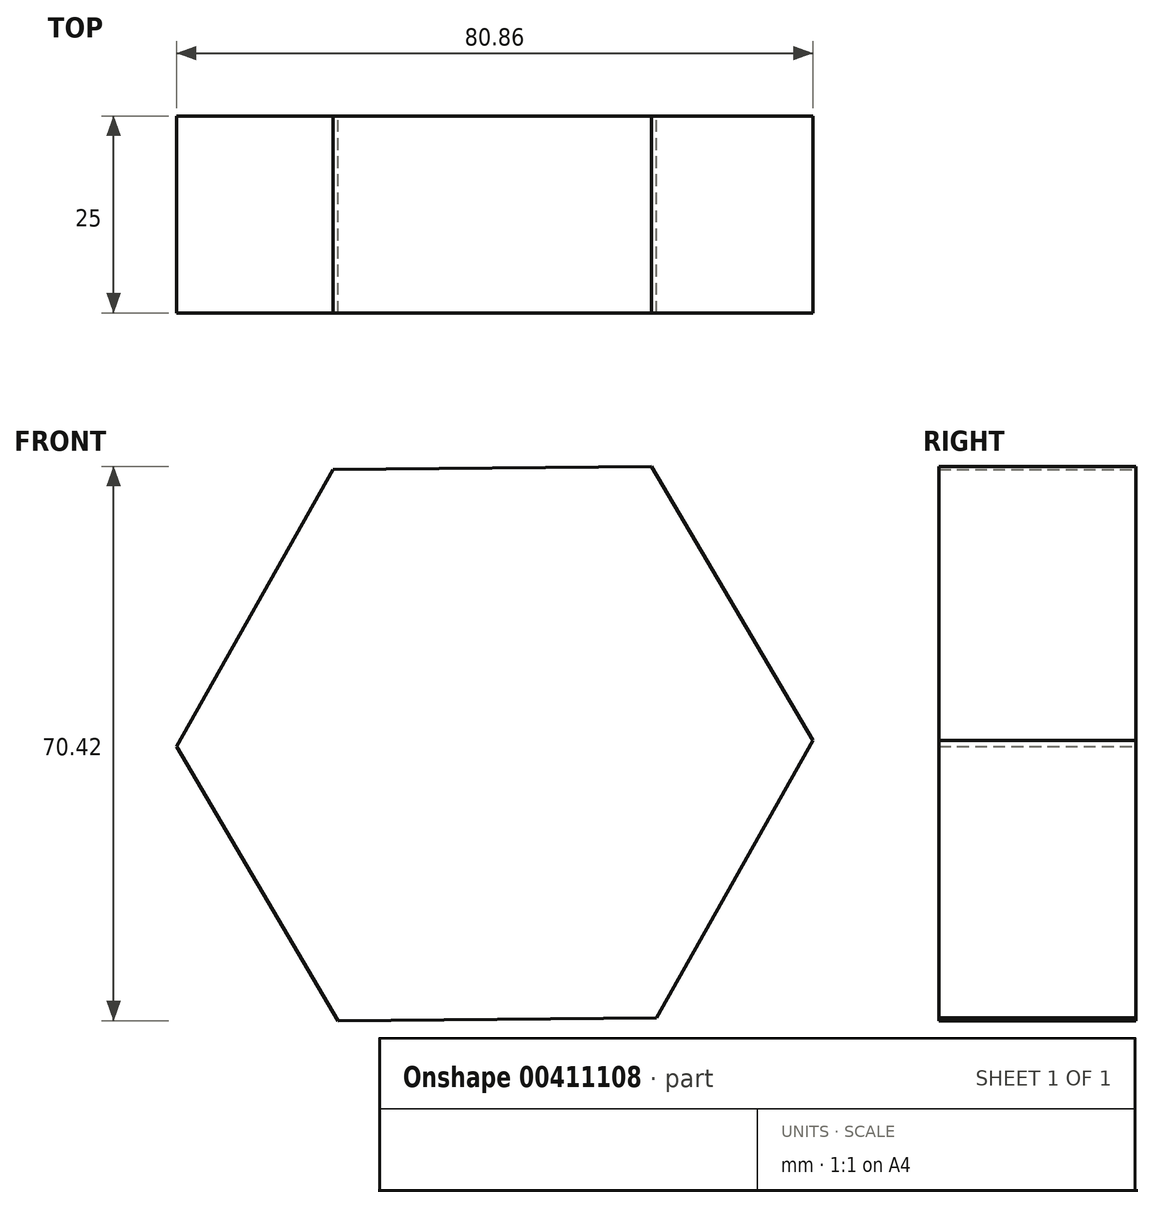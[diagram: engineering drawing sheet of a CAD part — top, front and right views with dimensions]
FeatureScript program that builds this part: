
annotation { "Feature Type Name" : "Feature", "Feature Type Description" : "" }
export const myFeature = defineFeature(function(context is Context, id is Id, definition is map)
    precondition{}
    {
        {
            var Q0;
            Q0=qCreatedBy(makeId("Front.planeOp"),FACE);
            var sketch = newSketch(context, id + "F0", { "sketchPlane" : qUnion([Q0])});
            skCircle(sketch, "E0", {"center": v(-53, 29.3) * mm, "radius": 40 * mm});
            skLineSegment(sketch, "E1.bottom", {"start": v(-12.08, 51.29) * mm, "end": v(0, 51.29) * mm});
            skLineSegment(sketch, "E1.top", {"start": v(-12.08, -74.46) * mm, "end": v(0, -74.46) * mm});
            skLineSegment(sketch, "E1.left", {"start": v(-12.08, 51.29) * mm, "end": v(-12.08, -74.46) * mm});
            skLineSegment(sketch, "E1.right", {"start": v(0, 51.29) * mm, "end": v(0, -74.46) * mm});
            skPoint(sketch, "E2.orphan", {"position": v(-12.08, -11.59) * mm});
            skLineSegment(sketch, "E3.left", {"start": v(-12.08, -11.59) * mm, "end": v(-12.08, 13.26) * mm});
            skPoint(sketch, "E3.middle", {"position": v(-24.88, 0.84) * mm});
            skLineSegment(sketch, "E4.0", {"start": v(-72.88, -5.92) * mm, "end": v(-93.42, 28.9) * mm});
            skLineSegment(sketch, "E4.1", {"start": v(-93.42, 28.9) * mm, "end": v(-73.54, 64.12) * mm});
            skLineSegment(sketch, "E4.2", {"start": v(-73.54, 64.12) * mm, "end": v(-33.1, 64.5) * mm});
            skLineSegment(sketch, "E4.3", {"start": v(-33.1, 64.5) * mm, "end": v(-12.56, 29.67) * mm});
            skLineSegment(sketch, "E4.4", {"start": v(-12.56, 29.67) * mm, "end": v(-32.44, -5.53) * mm});
            skLineSegment(sketch, "E4.5", {"start": v(-32.44, -5.53) * mm, "end": v(-72.88, -5.92) * mm});
            skPoint(sketch, "E4.0.midPoint", {"position": v(-83.15, 11.5) * mm});
            skLineSegment(sketch, "E5", {"start": v(-32.44, -5.53) * mm, "end": v(-12.08, 6.48) * mm});
            skLineSegment(sketch, "E6", {"start": v(-12.08, 6.48) * mm, "end": v(-32.44, -5.53) * mm});
            skLineSegment(sketch, "E7", {"start": v(-32.44, -5.53) * mm, "end": v(-51.42, -16.73) * mm});
            skLineSegment(sketch, "E8", {"start": v(-51.42, -16.73) * mm, "end": v(-72.88, -5.92) * mm});
            skLineSegment(sketch, "E9.0", {"start": v(-37.41, 61.96) * mm, "end": v(-16.86, 27.13) * mm});
            skSolve(sketch);
        }
        {
            var Q0;
            {var subQ0=sQuery(id+"F0.wireOp",EDGE,"E0");var subQ1=makeQuery(id+"F0.imprint","INTERSECT",VERTEX,{"derivedFrom":[subQ0,sQuery(id+"F0.wireOp",EDGE,"cFNFvZNz-d46b-ASLS-Qc6U-PmH5xnYiagzZ")]});Q0=makeQuery(id+"F0.imprint","IMPRINT",FACE,{"disambiguationData":[TD([[makeQuery(id+"F0.imprint","IMPRINT",EDGE,{"disambiguationData":[TD([[subQ1,1.0]])],"derivedFrom":subQ0}),1.0]])]});}
            var Q1;
            {var subQ0=sQuery(id+"F0.wireOp",EDGE,"E1.left");var subQ1=sQuery(id+"F0.wireOp",EDGE,"E0");var subQ2=makeQuery(id+"F0.imprint","INTERSECT",VERTEX,{"disambiguationData":[OD(0.0)],"derivedFrom":[subQ1,subQ0]});Q1=makeQuery(id+"F0.imprint","IMPRINT",FACE,{"disambiguationData":[TD([[makeQuery(id+"F0.imprint","IMPRINT",EDGE,{"disambiguationData":[TD([[subQ2,1.0]])],"derivedFrom":subQ1}),1.0]])]});}
            var Q2;
            {var subQ0=sQuery(id+"F0.wireOp",EDGE,"cFNFvZNz-d46b-ASLS-Qc6U-PmH5xnYiagzZ");var subQ1=sQuery(id+"F0.wireOp",EDGE,"E0");var subQ2=makeQuery(id+"F0.imprint","INTERSECT",VERTEX,{"derivedFrom":[subQ1,subQ0]});Q2=makeQuery(id+"F0.imprint","IMPRINT",FACE,{"disambiguationData":[TD([[makeQuery(id+"F0.imprint","IMPRINT",EDGE,{"disambiguationData":[TD([[subQ2,-1.0]])],"derivedFrom":subQ1}),-1.0]])]});}
            var Q3;
            {var subQ3=sQuery(id+"F0.wireOp",EDGE,"IICF6Ew8-t1GV-zMsd-5ZgM-YvJbXeU4h0B7");Q3=makeQuery(id+"F0.imprint","IMPRINT",FACE,{"disambiguationData":[TD([[makeQuery(id+"F0.imprint","IMPRINT",EDGE,{"derivedFrom":subQ3}),-1.0]])]});}
            var Q4;
            {var subQ6=sQuery(id+"F0.wireOp",EDGE,"VdmRn4Ws-3Hum-d5d3-mZHg-6YXjEL8K129l");Q4=makeQuery(id+"F0.imprint","IMPRINT",FACE,{"disambiguationData":[TD([[makeQuery(id+"F0.imprint","IMPRINT",EDGE,{"derivedFrom":subQ6}),1.0]])]});}
            extrude(context, id + "F1", {"entities" : qUnion([Q0, Q1, Q2, Q3, Q4]), "depth" : 25 * mm});
        }
    });
